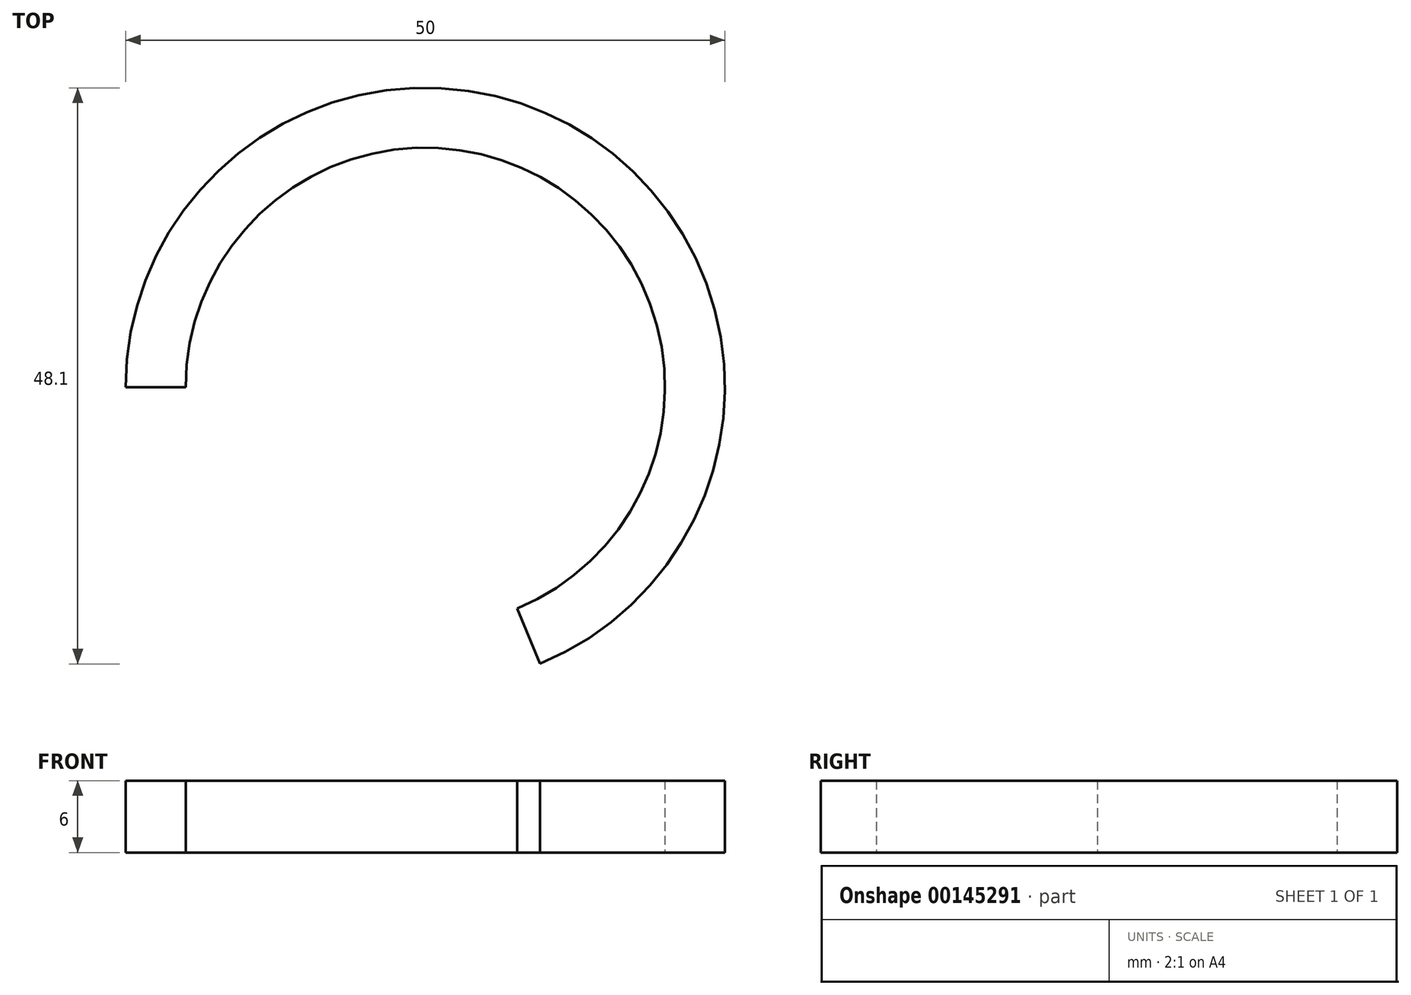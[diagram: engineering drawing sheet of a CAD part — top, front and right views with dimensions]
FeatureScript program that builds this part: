
annotation { "Feature Type Name" : "Feature", "Feature Type Description" : "" }
export const myFeature = defineFeature(function(context is Context, id is Id, definition is map)
    precondition{}
    {
        {
            var Q0;
            Q0=qCreatedBy(makeId("Top.planeOp"),FACE);
            var sketch = newSketch(context, id + "F0", { "sketchPlane" : qUnion([Q0])});
            skCircle(sketch, "E0", {"center": v(0, 0) * mm, "radius": 25 * mm});
            skLineSegment(sketch, "E1", {"start": v(0, 0) * mm, "end": v(-25, 0) * mm});
            skLineSegment(sketch, "E2", {"start": v(0, 0) * mm, "end": v(2.45, -5.9) * mm});
            skLineSegment(sketch, "E3", {"start": v(0, 0) * mm, "end": v(9.57, -23.1) * mm});
            skCircle(sketch, "E4", {"center": v(0, 0) * mm, "radius": 20 * mm});
            skSolve(sketch);
        }
        {
            var Q0;
            {var subQ0=sQuery(id+"F0.wireOp",EDGE,"E1");var subQ1=sQuery(id+"F0.wireOp",EDGE,"E0");var subQ2=makeQuery(id+"F0.imprint","INTERSECT",VERTEX,{"derivedFrom":[subQ1,subQ0]});Q0=makeQuery(id+"F0.imprint","IMPRINT",FACE,{"disambiguationData":[TD([[makeQuery(id+"F0.imprint","IMPRINT",EDGE,{"disambiguationData":[TD([[subQ2,1.0]])],"derivedFrom":subQ1}),1.0]])]});}
            extrude(context, id + "F1", {"entities" : qUnion([Q0]), "depth" : 6 * mm});
        }
    });
